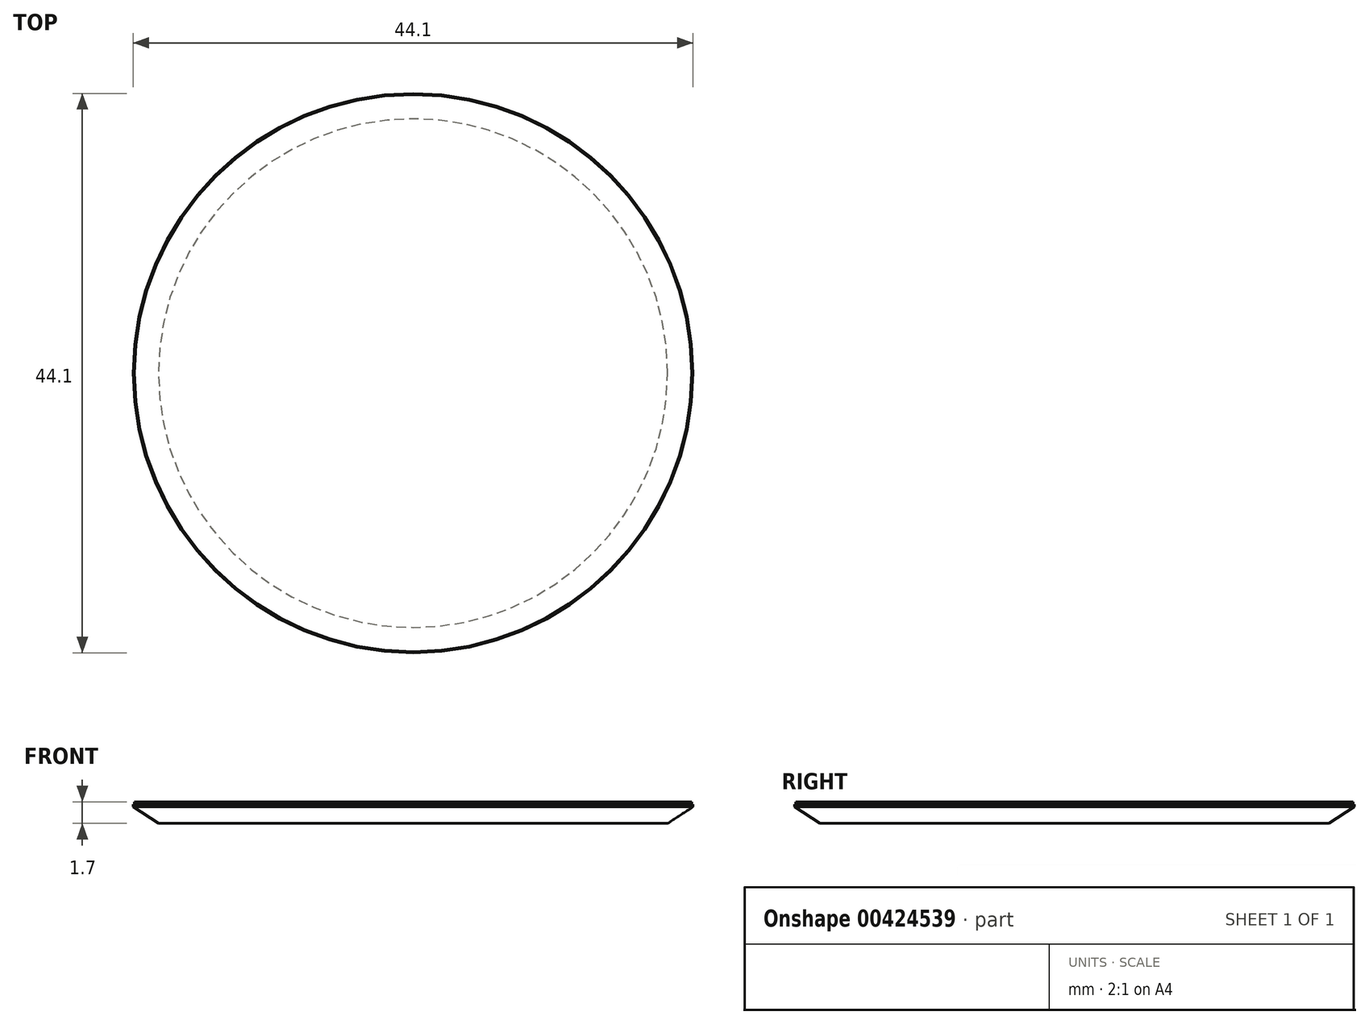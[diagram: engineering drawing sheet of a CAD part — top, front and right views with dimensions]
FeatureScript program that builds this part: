
annotation { "Feature Type Name" : "Feature", "Feature Type Description" : "" }
export const myFeature = defineFeature(function(context is Context, id is Id, definition is map)
    precondition{}
    {
        {
            var Q0;
            Q0=qCreatedBy(makeId("Top.planeOp"),FACE);
            var sketch = newSketch(context, id + "F0", { "sketchPlane" : qUnion([Q0])});
            skCircle(sketch, "E0", {"center": v(0, 0) * mm, "radius": 22.05 * mm});
            skSolve(sketch);
        }
        {
            var Q0;
            Q0=makeQuery(id+"F0.imprint","IMPRINT",FACE,{"disambiguationData":[TD([[makeQuery(id+"F0.imprint","IMPRINT",EDGE,{"derivedFrom":sQuery(id+"F0.wireOp",EDGE,"E0")}),1.0]])]});
            extrude(context, id + "F1", {"entities" : qUnion([Q0]), "oppositeDirection" : true, "depth" : 1.5 * mm});
        }
        {
            var Q0;
            Q0=makeQuery(id+"F1.opExtrude","CAP_EDGE",EDGE,{"disambiguationData":[OSD([sQuery(id+"F0.wireOp",EDGE,"E0")])],"isStart":false});
            chamfer(context, id + "F2", {"entities" : qUnion([Q0]), "chamferType" : ChamferType.TWO_OFFSETS, "width1" : 2 * mm, "oppositeDirection" : true, "width2" : 1.3 * mm, "tangentPropagation" : true});
        }
        {
            var Q0;
            Q0=makeQuery(id+"F1.opExtrude","CAP_FACE",FACE,{"disambiguationData":[OSD([sQuery(id+"F0.wireOp",EDGE,"E0")])],"isStart":true});
            var sketch = newSketch(context, id + "F3", { "sketchPlane" : qUnion([Q0])});
            skCircle(sketch, "E1", {"center": v(0, 0) * mm, "radius": 21.95 * mm});
            skSolve(sketch);
        }
        {
            var Q0;
            Q0=makeQuery(id+"F3.imprint","IMPRINT",FACE,{"disambiguationData":[TD([[makeQuery(id+"F3.imprint","IMPRINT",EDGE,{"derivedFrom":sQuery(id+"F3.wireOp",EDGE,"E1")}),1.0]])]});
            extrude(context, id + "F4", {"entities" : qUnion([Q0]), "operationType" : NewBodyOperationType.ADD, "depth" : .2 * mm});
        }
    });
